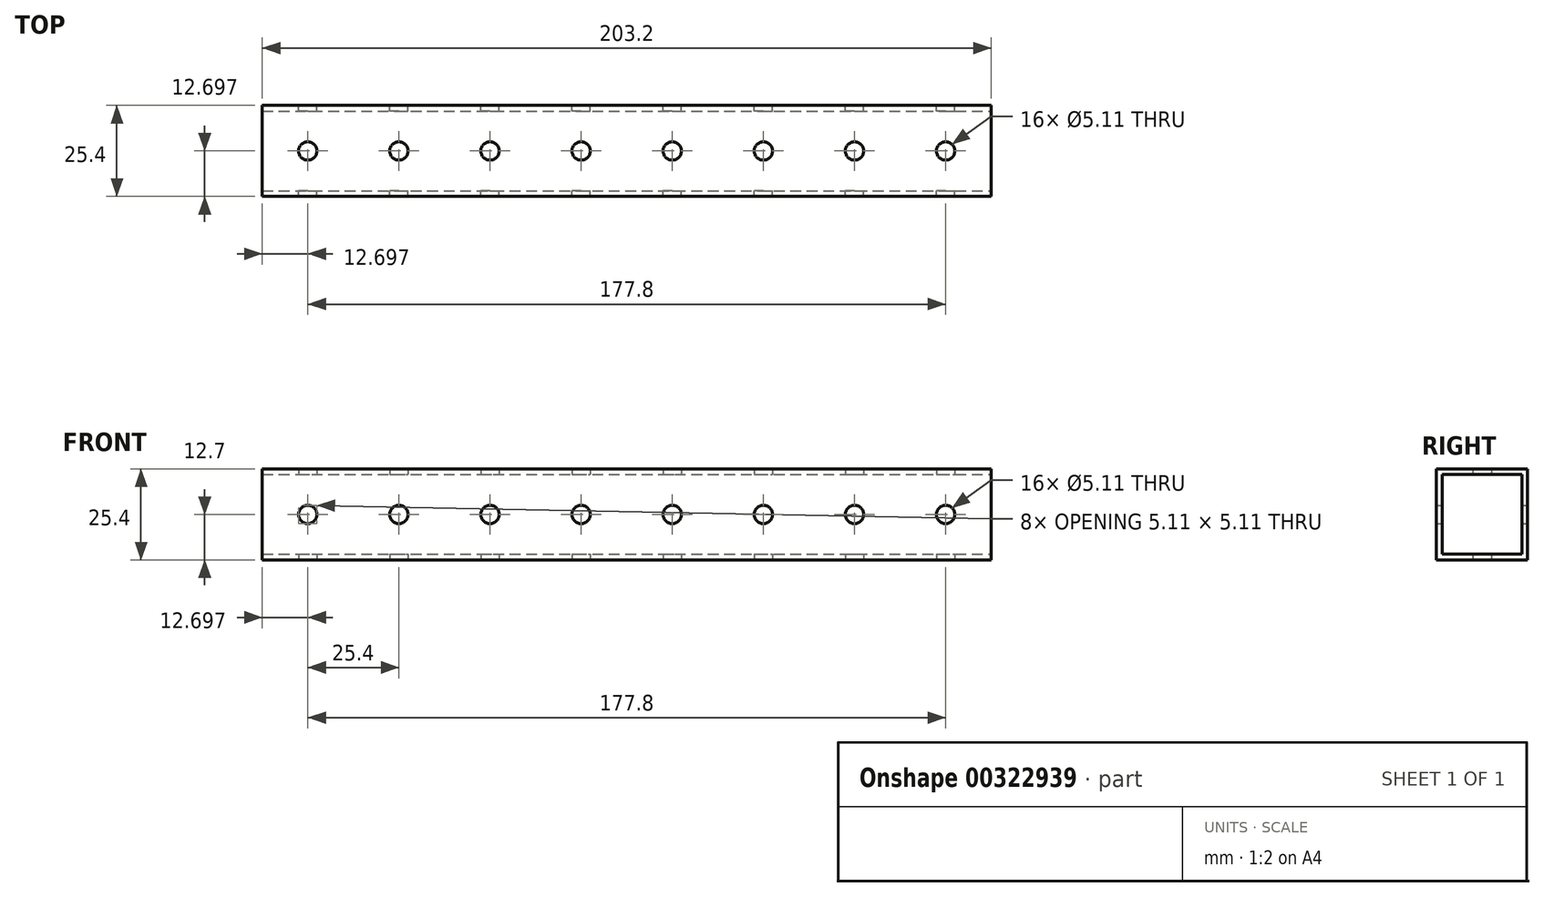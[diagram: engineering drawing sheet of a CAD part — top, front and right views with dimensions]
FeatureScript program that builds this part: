
annotation { "Feature Type Name" : "Feature", "Feature Type Description" : "" }
export const myFeature = defineFeature(function(context is Context, id is Id, definition is map)
    precondition{}
    {
        {
            var Q0;
            Q0=qCreatedBy(makeId("Top.planeOp"),FACE);
            var sketch = newSketch(context, id + "F0", { "sketchPlane" : qUnion([Q0])});
            skLineSegment(sketch, "E0.bottom", {"start": v(-109.06, 31.09) * mm, "end": v(94.14, 31.09) * mm});
            skLineSegment(sketch, "E0.top", {"start": v(-109.06, 5.69) * mm, "end": v(94.14, 5.69) * mm});
            skLineSegment(sketch, "E0.left", {"start": v(-109.06, 31.09) * mm, "end": v(-109.06, 5.69) * mm});
            skLineSegment(sketch, "E0.right", {"start": v(94.14, 31.09) * mm, "end": v(94.14, 5.69) * mm});
            skSolve(sketch);
        }
        {
            var Q0;
            Q0=makeQuery(id+"F0.imprint","IMPRINT",FACE,{"disambiguationData":[TD([[makeQuery(id+"F0.imprint","IMPRINT",EDGE,{"derivedFrom":sQuery(id+"F0.wireOp",EDGE,"E0.bottom")}),-1.0]])]});
            extrude(context, id + "F1", {"entities" : qUnion([Q0]), "depth" : 25.4 * mm});
        }
        {
            var Q0;
            Q0=makeQuery(id+"F1.opExtrude","SWEPT_FACE",FACE,{"disambiguationData":[OSD([sQuery(id+"F0.wireOp",EDGE,"E0.right")])]});
            var sketch = newSketch(context, id + "F2", { "sketchPlane" : qUnion([Q0])});
            skLineSegment(sketch, "E1.bottom", {"start": v(7.27, 23.81) * mm, "end": v(29.5, 23.81) * mm});
            skLineSegment(sketch, "E1.top", {"start": v(7.27, 1.6) * mm, "end": v(29.5, 1.6) * mm});
            skLineSegment(sketch, "E1.left", {"start": v(7.27, 23.81) * mm, "end": v(7.27, 1.6) * mm});
            skLineSegment(sketch, "E1.right", {"start": v(29.5, 23.81) * mm, "end": v(29.5, 1.6) * mm});
            skSolve(sketch);
        }
        {
            var Q0;
            Q0=makeQuery(id+"F2.imprint","IMPRINT",FACE,{"disambiguationData":[TD([[makeQuery(id+"F2.imprint","IMPRINT",EDGE,{"derivedFrom":sQuery(id+"F2.wireOp",EDGE,"E1.bottom")}),-1.0]])]});
            extrude(context, id + "F3", {"entities" : qUnion([Q0]), "operationType" : NewBodyOperationType.REMOVE, "oppositeDirection" : true, "depth" : 203.2 * mm});
        }
        {
            var Q0;
            Q0=makeQuery(id+"F1.opExtrude","CAP_FACE",FACE,{"disambiguationData":[OSD([sQuery(id+"F0.wireOp",EDGE,"E0.bottom"),sQuery(id+"F0.wireOp",EDGE,"E0.top"),sQuery(id+"F0.wireOp",EDGE,"E0.left"),sQuery(id+"F0.wireOp",EDGE,"E0.right")])],"isStart":false});
            var sketch = newSketch(context, id + "F4", { "sketchPlane" : qUnion([Q0])});
            skCircle(sketch, "E2", {"center": v(81.44, 18.39) * mm, "radius": 2.55 * mm});
            skCircle(sketch, "E3.0.1.0", {"center": v(81.44, -7.01) * mm, "radius": 2.55 * mm});
            skCircle(sketch, "E3.1.0.0", {"center": v(56.04, 18.39) * mm, "radius": 2.55 * mm});
            skCircle(sketch, "E3.1.1.0", {"center": v(56.04, -7.01) * mm, "radius": 2.55 * mm});
            skCircle(sketch, "E3.2.0.0", {"center": v(30.64, 18.39) * mm, "radius": 2.55 * mm});
            skCircle(sketch, "E3.2.1.0", {"center": v(30.64, -7.01) * mm, "radius": 2.55 * mm});
            skCircle(sketch, "E3.3.0.0", {"center": v(5.24, 18.39) * mm, "radius": 2.55 * mm});
            skCircle(sketch, "E3.3.1.0", {"center": v(5.24, -7.01) * mm, "radius": 2.55 * mm});
            skCircle(sketch, "E3.4.0.0", {"center": v(-20.16, 18.39) * mm, "radius": 2.55 * mm});
            skCircle(sketch, "E3.4.1.0", {"center": v(-20.16, -7.01) * mm, "radius": 2.55 * mm});
            skCircle(sketch, "E3.5.0.0", {"center": v(-45.56, 18.39) * mm, "radius": 2.55 * mm});
            skCircle(sketch, "E3.5.1.0", {"center": v(-45.56, -7.01) * mm, "radius": 2.55 * mm});
            skCircle(sketch, "E3.6.0.0", {"center": v(-70.96, 18.39) * mm, "radius": 2.55 * mm});
            skCircle(sketch, "E3.6.1.0", {"center": v(-70.96, -7.01) * mm, "radius": 2.55 * mm});
            skCircle(sketch, "E3.7.0.0", {"center": v(-96.36, 18.39) * mm, "radius": 2.55 * mm});
            skCircle(sketch, "E3.7.1.0", {"center": v(-96.36, -7.01) * mm, "radius": 2.55 * mm});
            skLineSegment(sketch, "E3.direction1", {"start": v(81.44, 18.39) * mm, "end": v(56.04, 18.39) * mm, "construction": true});
            skLineSegment(sketch, "E3.direction2", {"start": v(81.44, 18.39) * mm, "end": v(81.44, -7.01) * mm, "construction": true});
            skSolve(sketch);
        }
        {
            var Q0;
            Q0=makeQuery(id+"F1.opExtrude","SWEPT_FACE",FACE,{"disambiguationData":[OSD([sQuery(id+"F0.wireOp",EDGE,"E0.bottom")])]});
            var sketch = newSketch(context, id + "F5", { "sketchPlane" : qUnion([Q0])});
            skCircle(sketch, "E4", {"center": v(-81.44, 12.7) * mm, "radius": 2.55 * mm});
            skCircle(sketch, "E5.1.0.0", {"center": v(-56.04, 12.7) * mm, "radius": 2.55 * mm});
            skCircle(sketch, "E5.2.0.0", {"center": v(-30.64, 12.7) * mm, "radius": 2.55 * mm});
            skCircle(sketch, "E5.3.0.0", {"center": v(-5.24, 12.7) * mm, "radius": 2.55 * mm});
            skCircle(sketch, "E5.4.0.0", {"center": v(20.16, 12.7) * mm, "radius": 2.55 * mm});
            skCircle(sketch, "E5.5.0.0", {"center": v(45.56, 12.7) * mm, "radius": 2.55 * mm});
            skCircle(sketch, "E5.6.0.0", {"center": v(70.96, 12.7) * mm, "radius": 2.55 * mm});
            skCircle(sketch, "E5.7.0.0", {"center": v(96.36, 12.7) * mm, "radius": 2.55 * mm});
            skLineSegment(sketch, "E5.direction1", {"start": v(-81.44, 12.7) * mm, "end": v(-56.04, 12.7) * mm, "construction": true});
            skSolve(sketch);
        }
        {
            var Q0;
            Q0=makeQuery(id+"F5.imprint","IMPRINT",FACE,{"disambiguationData":[TD([[makeQuery(id+"F5.imprint","IMPRINT",EDGE,{"derivedFrom":sQuery(id+"F5.wireOp",EDGE,"E5.3.0.0")}),1.0]])]});
            var Q1;
            Q1=makeQuery(id+"F5.imprint","IMPRINT",FACE,{"disambiguationData":[TD([[makeQuery(id+"F5.imprint","IMPRINT",EDGE,{"derivedFrom":sQuery(id+"F5.wireOp",EDGE,"E5.2.0.0")}),1.0]])]});
            var Q2;
            Q2=makeQuery(id+"F5.imprint","IMPRINT",FACE,{"disambiguationData":[TD([[makeQuery(id+"F5.imprint","IMPRINT",EDGE,{"derivedFrom":sQuery(id+"F5.wireOp",EDGE,"E5.4.0.0")}),1.0]])]});
            var Q3;
            Q3=makeQuery(id+"F5.imprint","IMPRINT",FACE,{"disambiguationData":[TD([[makeQuery(id+"F5.imprint","IMPRINT",EDGE,{"derivedFrom":sQuery(id+"F5.wireOp",EDGE,"E5.5.0.0")}),1.0]])]});
            var Q4;
            Q4=makeQuery(id+"F5.imprint","IMPRINT",FACE,{"disambiguationData":[TD([[makeQuery(id+"F5.imprint","IMPRINT",EDGE,{"derivedFrom":sQuery(id+"F5.wireOp",EDGE,"E5.6.0.0")}),1.0]])]});
            var Q5;
            Q5=makeQuery(id+"F5.imprint","IMPRINT",FACE,{"disambiguationData":[TD([[makeQuery(id+"F5.imprint","IMPRINT",EDGE,{"derivedFrom":sQuery(id+"F5.wireOp",EDGE,"E5.7.0.0")}),1.0]])]});
            var Q6;
            Q6=makeQuery(id+"F5.imprint","IMPRINT",FACE,{"disambiguationData":[TD([[makeQuery(id+"F5.imprint","IMPRINT",EDGE,{"derivedFrom":sQuery(id+"F5.wireOp",EDGE,"E4")}),1.0]])]});
            var Q7;
            Q7=makeQuery(id+"F5.imprint","IMPRINT",FACE,{"disambiguationData":[TD([[makeQuery(id+"F5.imprint","IMPRINT",EDGE,{"derivedFrom":sQuery(id+"F5.wireOp",EDGE,"E5.1.0.0")}),1.0]])]});
            extrude(context, id + "F6", {"entities" : qUnion([Q0, Q1, Q2, Q3, Q4, Q5, Q6, Q7]), "operationType" : NewBodyOperationType.REMOVE, "oppositeDirection" : true, "depth" : 50.8 * mm});
        }
        {
            var Q0;
            Q0=sQuery(id+"F4.wireOp",VERTEX,"E3.0.1.0.center");
            var Q1;
            Q1=sQuery(id+"F4.wireOp",VERTEX,"E3.7.0.0.center");
            var Q2;
            Q2=sQuery(id+"F4.wireOp",VERTEX,"E3.6.0.0.center");
            var Q3;
            Q3=sQuery(id+"F4.wireOp",VERTEX,"E3.2.0.0.center");
            var Q4;
            Q4=sQuery(id+"F4.wireOp",VERTEX,"E3.7.1.0.center");
            var Q5;
            Q5=sQuery(id+"F4.wireOp",VERTEX,"E3.4.0.0.center");
            var Q6;
            Q6=sQuery(id+"F4.wireOp",VERTEX,"E2.center");
            var Q7;
            Q7=sQuery(id+"F4.wireOp",VERTEX,"E3.5.1.0.center");
            var Q8;
            Q8=sQuery(id+"F4.wireOp",VERTEX,"E3.3.1.0.center");
            var Q9;
            Q9=sQuery(id+"F4.wireOp",VERTEX,"E3.1.1.0.center");
            var Q10;
            Q10=sQuery(id+"F4.wireOp",VERTEX,"E3.2.1.0.center");
            var Q11;
            Q11=sQuery(id+"F4.wireOp",VERTEX,"E3.1.0.0.center");
            var Q12;
            Q12=sQuery(id+"F4.wireOp",VERTEX,"E3.5.0.0.center");
            var Q13;
            Q13=sQuery(id+"F4.wireOp",VERTEX,"E3.6.1.0.center");
            var Q14;
            Q14=sQuery(id+"F4.wireOp",VERTEX,"E3.4.1.0.center");
            var Q15;
            Q15=sQuery(id+"F4.wireOp",VERTEX,"E3.3.0.0.center");
            var Q16;
            Q16=makeQuery(id+"F1.opExtrude","SWEPT_BODY",BODY,{"disambiguationData":[OSD([sQuery(id+"F0.wireOp",EDGE,"E0.bottom"),sQuery(id+"F0.wireOp",EDGE,"E0.top"),sQuery(id+"F0.wireOp",EDGE,"E0.left"),sQuery(id+"F0.wireOp",EDGE,"E0.right")])]});
            hole(context, id + "F7", {"style" : HoleStyle.SIMPLE, "endStyle" : HoleEndStyle.THROUGH, "holeDiameter" : 5.1 * mm, "tappedDepth" : 12.7 * mm, "tapClearance" : 3, "locations" : qUnion([Q0, Q1, Q2, Q3, Q4, Q5, Q6, Q7, Q8, Q9, Q10, Q11, Q12, Q13, Q14, Q15]), "scope" : qUnion([Q16])});
        }
    });
